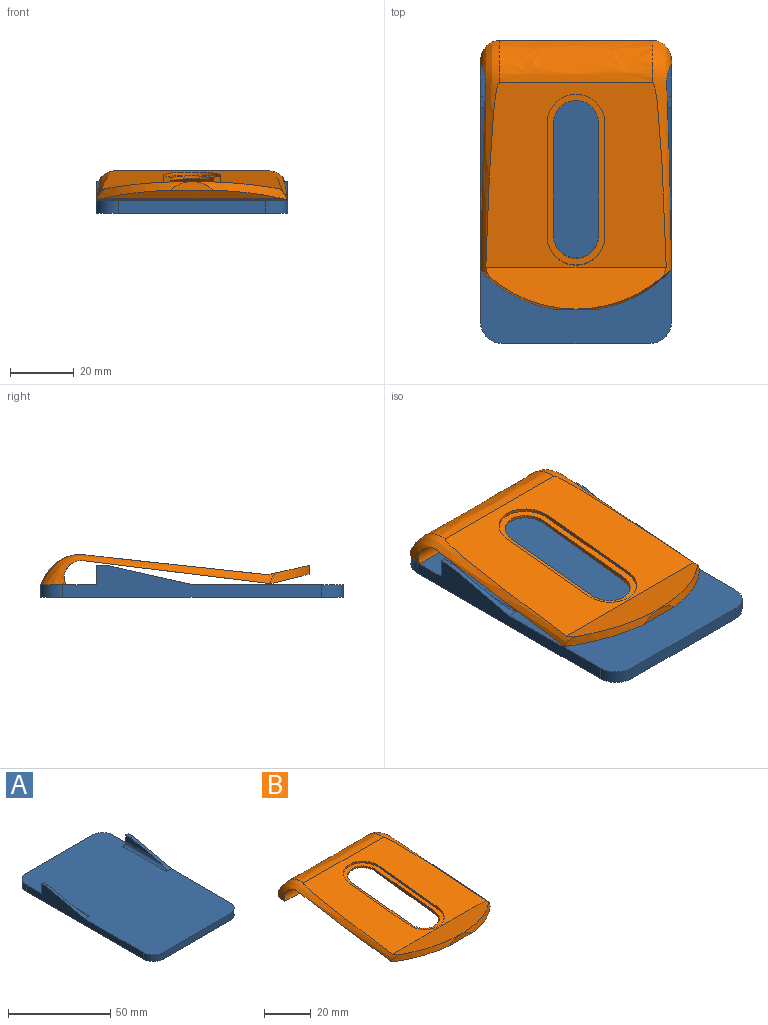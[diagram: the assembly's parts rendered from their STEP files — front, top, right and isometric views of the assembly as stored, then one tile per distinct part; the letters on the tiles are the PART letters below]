
ASSEMBLY  parts=2 mates=1
PART A: 33 faces, bbox 60x95x10 mm
  f0: plane 95x60mm, normal (0,0,1), area 5447.9mm2, adj f2,f3,f4,f9,f18,f19,f20,f21
  f1: plane 95x60mm, normal (0,0,-1), area 2911.4mm2, adj f2,f3,f4,f5,f6,f7,f8,f9
  f2: plane 46x4mm, normal (0,-1,0), area 184mm2, adj f0,f1,f18,f19
  f3: plane 81x10mm, normal (1,0,0), area 424.4mm2, adj f0,f1,f18,f20,f25,f27,f28
  f4: plane 46x4mm, normal (0,1,0), area 184mm2, adj f0,f1,f20,f21
  f5: extruded ~28.27x20.59mm, area 134.8mm2, adj f1,f6,f8,f32
  f6: extruded ~41.31x21.8mm, area 191.5mm2, adj f1,f5,f7,f32
  f7: extruded ~41.31x21.8mm, area 191.5mm2, adj f1,f6,f8,f32
  f8: extruded ~28.27x20.59mm, area 134.8mm2, adj f1,f5,f7,f32
  f9: plane 81x10mm, normal (-1,0,0), area 424.4mm2, adj f0,f1,f19,f21,f22,f24,f29
  f10: cylinder r=4.25mm len=8.5mm, axis (0,0,1), area 80.1mm2, adj f1,f16
  f11: cylinder r=4.25mm len=8.5mm, axis (0,0,1), area 80.1mm2, adj f1,f15
  f12: cylinder r=4.25mm len=8.5mm, axis (0,0,1), area 80.1mm2, adj f1,f17
  f13: cylinder r=4.25mm len=8.5mm, axis (0,0,1), area 80.1mm2, adj f1,f14
  f14: plane 8.5x8.5mm, normal (0,0,-1), area 56.7mm2, adj f13
  f15: plane 8.5x8.5mm, normal (0,0,-1), area 56.7mm2, adj f11
  f16: plane 8.5x8.5mm, normal (0,0,-1), area 56.7mm2, adj f10
  f17: plane 8.5x8.5mm, normal (0,0,-1), area 56.7mm2, adj f12
  f18: cylinder r=7mm len=7mm, axis (0,0,1), area 44mm2, adj f0,f1,f2,f3
  f19: cylinder r=7mm len=7mm, axis (0,0,-1), area 44mm2, adj f0,f1,f2,f9
  f20: cylinder r=7mm len=7mm, axis (0,0,-1), area 44mm2, adj f0,f1,f3,f4
  f21: cylinder r=7mm len=7mm, axis (0,0,1), area 44mm2, adj f0,f1,f4,f9
  f22: plane 6x3.5mm, normal (0,1,0), area 9.9mm2, adj f0,f9,f23,f24,f31
  f23: plane 21.16x4mm, normal (1,0,0), area 49.2mm2, adj f22,f24,f29,f31
  f24: plane 3.47x1.5mm, normal (0,0,1), area 5.2mm2, adj f9,f22,f23,f29
  f25: plane 6x3.5mm, normal (0,1,0), area 9.9mm2, adj f0,f3,f26,f27,f30
  f26: plane 21.16x4mm, normal (-1,0,0), area 49.2mm2, adj f25,f27,f28,f30
  f27: plane 3.47x1.5mm, normal (0,0,1), area 5.2mm2, adj f3,f25,f26,f28
  f28: plane 26.53x6mm, normal (0,-0.22,0.98), area 44.7mm2, adj f0,f3,f26,f27,f30
  f29: plane 26.53x6mm, normal (0,-0.22,0.98), area 44.7mm2, adj f0,f9,f23,f24,f31
  f30: cylinder r=2mm len=30mm, axis (0,-1,0), area 84.2mm2, adj f0,f25,f26,f28
  f31: cylinder r=2mm len=30mm, axis (0,1,0), area 84.2mm2, adj f0,f22,f23,f29
  f32: plane 69.58x43.63mm, normal (0,0,-1), area 2519.5mm2, adj f5,f6,f7,f8
PART B: 25 faces, bbox 60.2x85.3x12.6 mm
  f0: plane 35.67x5.35mm, normal (-1,0,0), area 45.3mm2, adj f1,f3,f4,f24
  f1: cylinder r=7.04mm len=14.08mm, axis (0,-0.11,0.99), area 22.5mm2, adj f0,f2,f4,f24
  f2: plane 35.67x5.35mm, normal (1,0,0), area 45.3mm2, adj f1,f3,f4,f24
  f3: cylinder r=7.04mm len=14.08mm, axis (0,-0.11,0.99), area 33.5mm2, adj f0,f2,f4,f24
  f4: plane 59.8x58.08mm, normal (0,0.12,-0.99), area 2747.9mm2, adj f0,f1,f2,f3,f13,f17,f18,f19
  f5: plane 57.92x56.56mm, normal (0,-0.11,0.99), area 2236.9mm2, adj f12,f14,f17,f18,f20,f21,f22,f23
  f6: plane 13.79x2.71mm, normal (0,-1,0), area 25mm2, adj f7,f15,f16
  f7: plane 56.04x10.39mm, normal (0,-0.24,-0.97), area 426.4mm2, adj f6,f8,f15,f16
  f8: plane 57.84x0.91mm, normal (0,-0.22,-0.98), area 52.9mm2, adj f7,f15,f16,f19
  f9: plane 1.03x0.93mm, normal (-1,0,0), area 0.5mm2, adj f11,f13,f18
  f10: plane 1.03x0.93mm, normal (1,0,0), area 0.5mm2, adj f11,f13,f17
  f11: plane 60x7.93mm, normal (0,0,-1), area 458.7mm2, adj f9,f10,f13,f14,f17,f18
  f12: plane 56.63x13.04mm, normal (0,0.22,0.98), area 547.3mm2, adj f5,f15,f16,f17,f18
  f13: cylinder r=5.32mm len=60mm, axis (-1,0,0), area 659.1mm2, adj f4,f9,f10,f11,f17,f18
  f14: extruded ~48x13.33mm, area 836.4mm2, adj f5,f11,f17,f18
  f15: cylinder r=40.5mm len=29.79mm, axis (0,0.22,0.98), area 75.4mm2, adj f6,f7,f8,f12,f17,f19
  f16: cylinder r=40.5mm len=29.79mm, axis (0,0.22,0.98), area 75.4mm2, adj f6,f7,f8,f12,f18,f19
  f17: bspline ~81.48x12.45mm, area 300.7mm2, adj f4,f5,f10,f11,f12,f13,f14,f15
  f18: bspline ~81.48x12.45mm, area 300.7mm2, adj f4,f5,f9,f11,f12,f13,f14,f16
  f19: cylinder r=5mm len=59.6mm, axis (-1,0,0), area 100.9mm2, adj f4,f8,f15,f16,f17,f18
  f20: cylinder r=9.04mm len=18.08mm, axis (0,-0.11,0.99), area 28.4mm2, adj f5,f21,f23,f24
  f21: plane 35.66x4.84mm, normal (1,0,0), area 35.8mm2, adj f5,f20,f22,f24
  f22: cylinder r=9.04mm len=18.08mm, axis (0,-0.11,0.99), area 28.4mm2, adj f5,f21,f23,f24
  f23: plane 35.66x4.84mm, normal (-1,0,0), area 35.8mm2, adj f5,f20,f22,f24
  f24: plane 53.53x18.08mm, normal (0,-0.11,0.99), area 244.1mm2, adj f0,f1,f2,f3,f20,f21,f22,f23
PLACE A t=(64.16,-11.52,0)mm
PLACE B t=(64.16,-11.52,0)mm
MATE fastened A.f0 <-> B.f11  axis (0,0,1) through (64.16,35.98,4)mm
